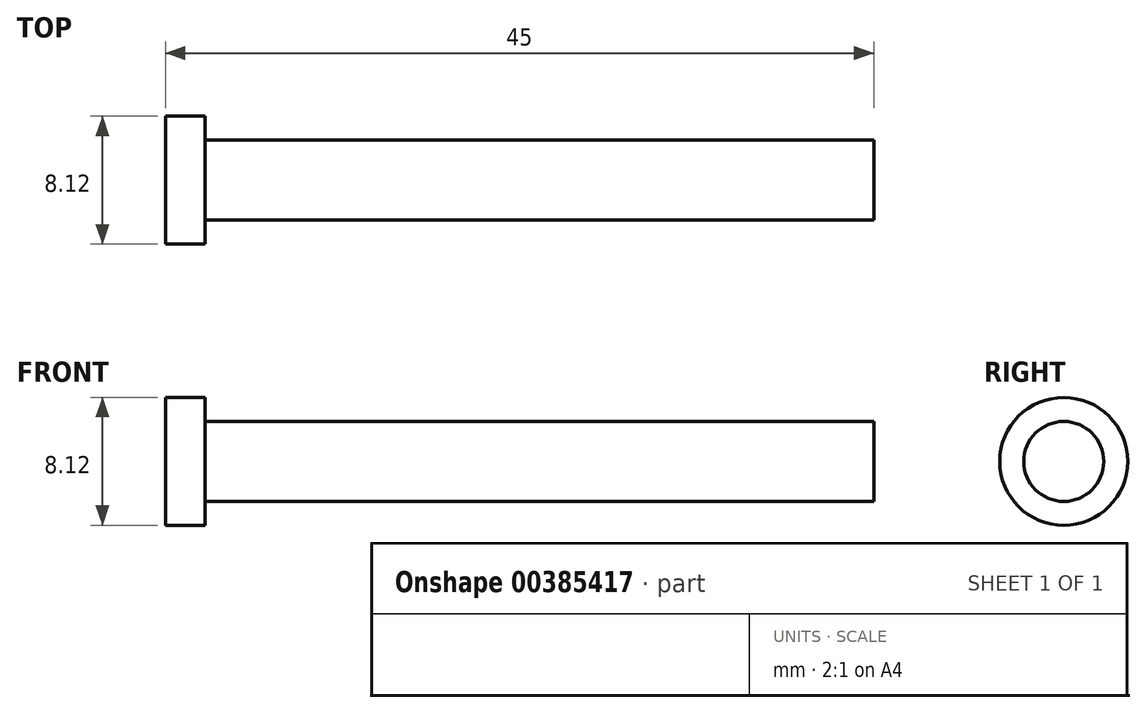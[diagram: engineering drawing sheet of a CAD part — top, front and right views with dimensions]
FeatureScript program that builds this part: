
annotation { "Feature Type Name" : "Feature", "Feature Type Description" : "" }
export const myFeature = defineFeature(function(context is Context, id is Id, definition is map)
    precondition{}
    {
        {
            var Q0;
            Q0=qCreatedBy(makeId("Front.planeOp"),FACE);
            var sketch = newSketch(context, id + "F0", { "sketchPlane" : qUnion([Q0])});
            skLineSegment(sketch, "E0", {"start": v(23.57, 28.66) * mm, "end": v(-18.89, 28.66) * mm});
            skLineSegment(sketch, "E1", {"start": v(-18.89, 28.66) * mm, "end": v(-18.89, 30.18) * mm});
            skLineSegment(sketch, "E2", {"start": v(-18.89, 30.18) * mm, "end": v(-21.43, 30.18) * mm});
            skLineSegment(sketch, "E3", {"start": v(-21.43, 30.18) * mm, "end": v(-21.43, 26.12) * mm});
            skLineSegment(sketch, "E4", {"start": v(-21.43, 26.12) * mm, "end": v(23.57, 26.12) * mm});
            skLineSegment(sketch, "E5", {"start": v(23.57, 26.12) * mm, "end": v(23.57, 28.66) * mm});
            skSolve(sketch);
        }
        {
            var Q0;
            Q0=makeQuery(id+"F0.imprint","IMPRINT",FACE,{"disambiguationData":[TD([[makeQuery(id+"F0.imprint","IMPRINT",EDGE,{"derivedFrom":sQuery(id+"F0.wireOp",EDGE,"E0")}),1.0]])]});
            var Q1;
            Q1=sQuery(id+"F0.wireOp",EDGE,"E4");
            revolve(context, id + "F1", {"entities" : qUnion([Q0]), "axis" : qUnion([Q1]), "revolveType" : RevolveType.FULL});
        }
    });
